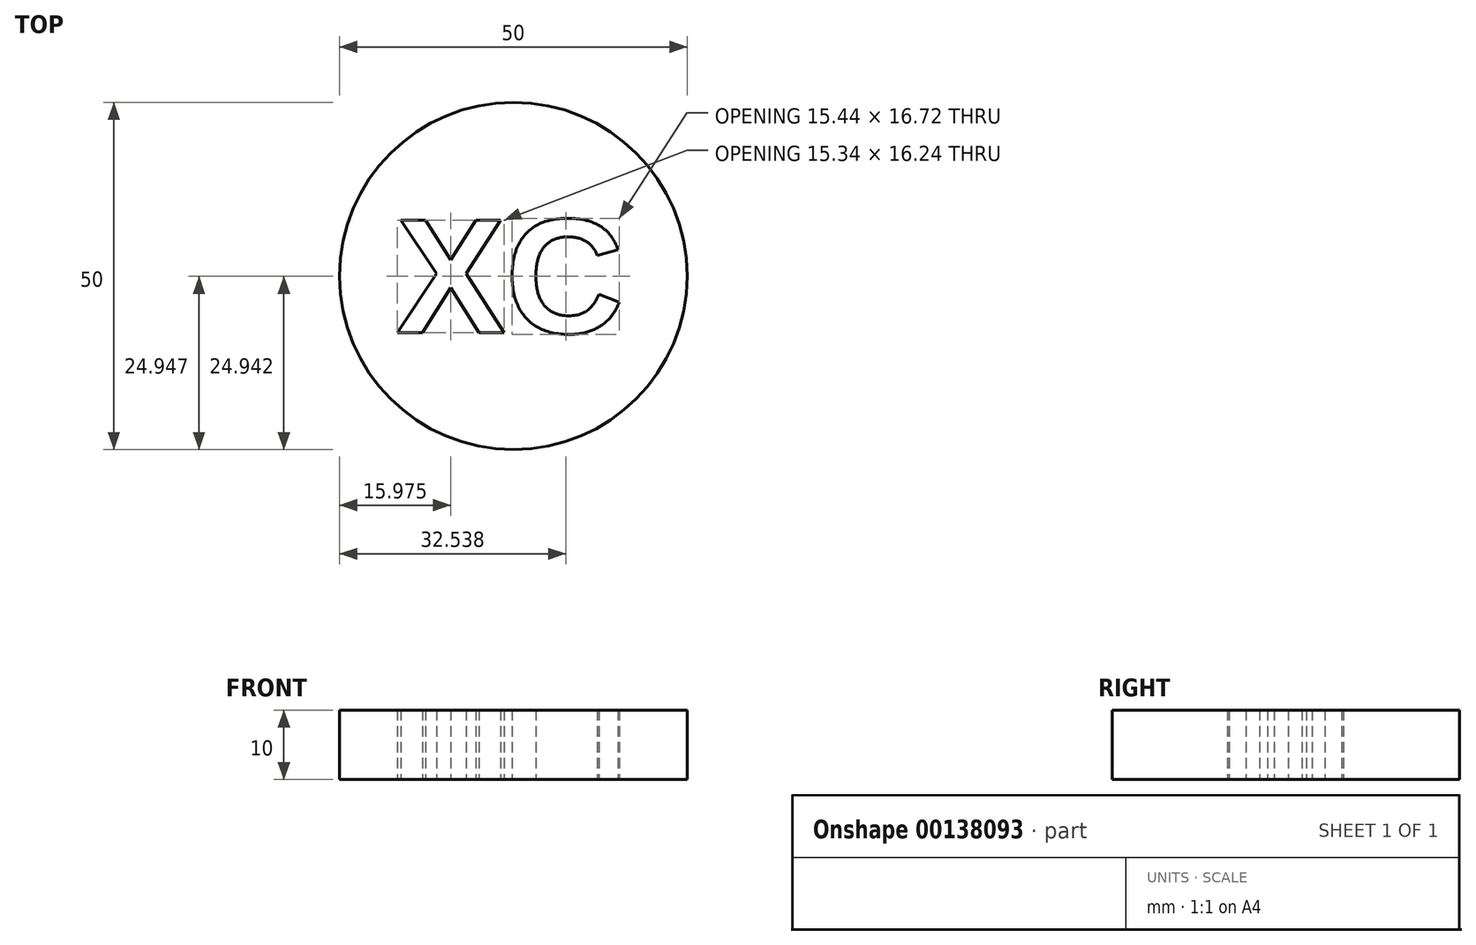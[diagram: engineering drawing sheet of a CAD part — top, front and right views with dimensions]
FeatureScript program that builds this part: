
annotation { "Feature Type Name" : "Feature", "Feature Type Description" : "" }
export const myFeature = defineFeature(function(context is Context, id is Id, definition is map)
    precondition{}
    {
        {
            var Q0;
            Q0=qCreatedBy(makeId("Top.planeOp"),FACE);
            var sketch = newSketch(context, id + "F0", { "sketchPlane" : qUnion([Q0])});
            skCircle(sketch, "E0", {"center": v(0, 0) * mm, "radius": 25 * mm});
            skText(sketch, "E1", { "text": "XC", "fontName": "Arimo-Bold.ttf"});
            const initialGuessF0  = {"E1": [-0.0169, -0.00818, 1, 0, 0.017]};
            skSetInitialGuess(sketch, initialGuessF0);
            skSolve(sketch);
        }
        {
            var Q0;
            Q0=makeQuery(id+"F0.imprint","IMPRINT",FACE,{"disambiguationData":[TD([[makeQuery(id+"F0.imprint","IMPRINT",EDGE,{"derivedFrom":sQuery(id+"F0.wireOp",EDGE,"E0")}),1.0]])]});
            extrude(context, id + "F1", {"entities" : qUnion([Q0]), "depth" : 10 * mm});
        }
    });
